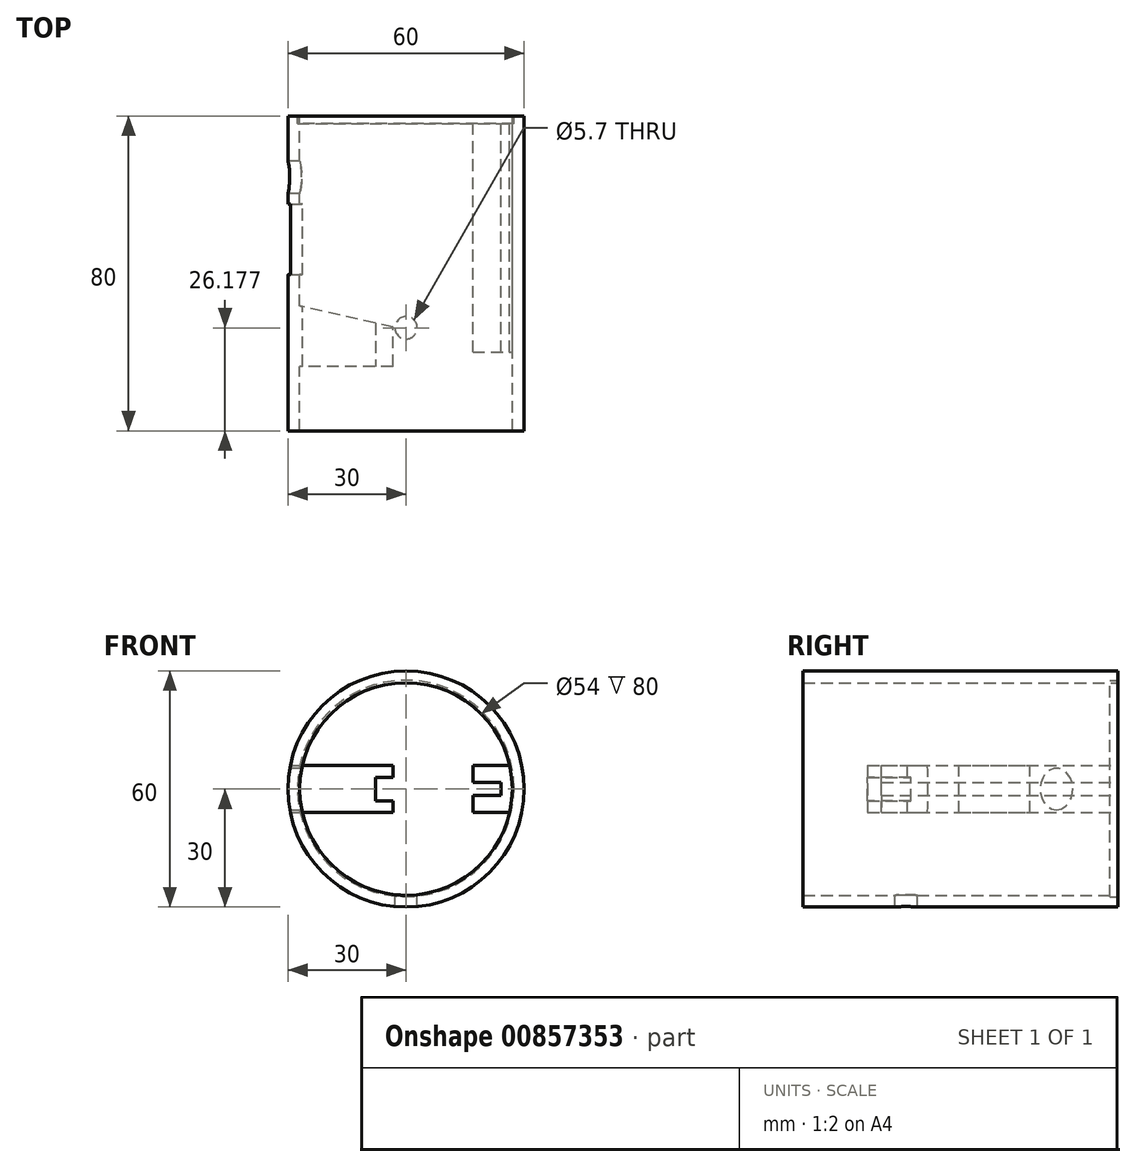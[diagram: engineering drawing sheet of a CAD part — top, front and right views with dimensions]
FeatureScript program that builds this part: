
annotation { "Feature Type Name" : "Feature", "Feature Type Description" : "" }
export const myFeature = defineFeature(function(context is Context, id is Id, definition is map)
    precondition{}
    {
        {
            var Q0;
            Q0=qCreatedBy(makeId("Front.planeOp"),FACE);
            var sketch = newSketch(context, id + "F0", { "sketchPlane" : qUnion([Q0])});
            skCircle(sketch, "E0", {"center": v(0, 0) * mm, "radius": 30 * mm});
            skCircle(sketch, "E1", {"center": v(0, 0) * mm, "radius": 27 * mm});
            skLineSegment(sketch, "E2.bottom", {"start": v(17, 0) * mm, "end": v(27, 0) * mm});
            skLineSegment(sketch, "E2.top", {"start": v(17, -6) * mm, "end": v(26.32, -6) * mm});
            skLineSegment(sketch, "E2.left", {"start": v(17, 0) * mm, "end": v(17, -6) * mm});
            skLineSegment(sketch, "E3.MirrorCS", {"start": v(17, 0) * mm, "end": v(17, 6) * mm});
            skLineSegment(sketch, "E4.MirrorCS", {"start": v(17, 6) * mm, "end": v(26.32, 6) * mm});
            skLineSegment(sketch, "E5.bottom", {"start": v(17, 0) * mm, "end": v(24.16, 0) * mm});
            skLineSegment(sketch, "E5.top", {"start": v(17, -1.62) * mm, "end": v(24.16, -1.62) * mm});
            skLineSegment(sketch, "E5.left", {"start": v(17, 0) * mm, "end": v(17, -1.62) * mm});
            skLineSegment(sketch, "E5.right", {"start": v(24.16, 0) * mm, "end": v(24.16, -1.62) * mm});
            skLineSegment(sketch, "E6.MirrorCS", {"start": v(17, 1.62) * mm, "end": v(24.16, 1.62) * mm});
            skLineSegment(sketch, "E7.MirrorCS", {"start": v(24.16, 0) * mm, "end": v(24.16, 1.62) * mm});
            skSolve(sketch);
        }
        {
            var Q0;
            Q0=makeQuery(id+"F0.imprint","IMPRINT",FACE,{"disambiguationData":[TD([[makeQuery(id+"F0.imprint","IMPRINT",EDGE,{"derivedFrom":sQuery(id+"F0.wireOp",EDGE,"E0")}),1.0]])]});
            extrude(context, id + "F1", {"entities" : qUnion([Q0]), "depth" : 80 * mm});
        }
        {
            var Q0;
            Q0=qCreatedBy(makeId("Front.planeOp"),FACE);
            var sketch = newSketch(context, id + "F2", { "sketchPlane" : qUnion([Q0])});
            skCircle(sketch, "E8", {"center": v(-0.08, 0.14) * mm, "radius": 27.5 * mm});
            skSolve(sketch);
        }
        {
            var Q0;
            Q0=makeQuery(id+"F2.imprint","IMPRINT",FACE,{"disambiguationData":[TD([[makeQuery(id+"F2.imprint","IMPRINT",EDGE,{"derivedFrom":sQuery(id+"F2.wireOp",EDGE,"E8")}),1.0]])]});
            extrude(context, id + "F3", {"entities" : qUnion([Q0]), "offsetDistance" : 25 * mm, "depth" : 2 * mm});
        }
        {
            var Q0;
            Q0=qCreatedBy(makeId("Top.planeOp"),FACE);
            var sketch = newSketch(context, id + "F4", { "sketchPlane" : qUnion([Q0])});
            skLineSegment(sketch, "E9.bottom", {"start": v(-32.36, -22.34) * mm, "end": v(-18.81, -22.34) * mm});
            skLineSegment(sketch, "E9.top", {"start": v(-32.36, -40.34) * mm, "end": v(-18.81, -40.34) * mm});
            skLineSegment(sketch, "E9.left", {"start": v(-32.36, -22.34) * mm, "end": v(-32.36, -40.34) * mm});
            skLineSegment(sketch, "E9.right", {"start": v(-18.81, -22.34) * mm, "end": v(-18.81, -40.34) * mm});
            skSolve(sketch);
        }
        {
            var Q0;
            Q0=makeQuery(id+"F4.imprint","IMPRINT",FACE,{"disambiguationData":[TD([[makeQuery(id+"F4.imprint","IMPRINT",EDGE,{"derivedFrom":sQuery(id+"F4.wireOp",EDGE,"E9.bottom")}),-1.0]])]});
            var Q1;
            Q1=qSketchRegion(id+"F6",true);
            extrude(context, id + "F5", {"entities" : qUnion([Q0, Q1]), "operationType" : NewBodyOperationType.REMOVE, "endBound" : BoundingType.SYMMETRIC, "depth" : 12 * mm, "hasSecondDirection" : true, "secondDirectionOppositeDirection" : true, "secondDirectionDepth" : 4.6 * mm});
        }
        {
            var Q0;
            Q0=qCreatedBy(makeId("Top.planeOp"),FACE);
            var sketch = newSketch(context, id + "F6", { "sketchPlane" : qUnion([Q0])});
            skCircle(sketch, "E10", {"center": v(0, -53.82) * mm, "radius": 2.85 * mm});
            skSolve(sketch);
        }
        {
            var Q0;
            Q0=makeQuery(id+"F6.imprint","IMPRINT",FACE,{"disambiguationData":[TD([[makeQuery(id+"F6.imprint","IMPRINT",EDGE,{"derivedFrom":sQuery(id+"F6.wireOp",EDGE,"E10")}),1.0]])]});
            var Q1;
            Q1=sQuery(id+"F6.wireOp",EDGE,"E10");
            extrude(context, id + "F7", {"entities" : qUnion([Q0]), "operationType" : NewBodyOperationType.REMOVE, "surfaceEntities" : qUnion([Q1]), "oppositeDirection" : true, "depth" : 34.4 * mm});
        }
        {
            var Q0;
            Q0=qCreatedBy(makeId("Top.planeOp"),FACE);
            var sketch = newSketch(context, id + "F8", { "sketchPlane" : qUnion([Q0])});
            skLineSegment(sketch, "E11.bottom", {"start": v(-3.31, -63.62) * mm, "end": v(-27.31, -63.62) * mm});
            skLineSegment(sketch, "E11.top", {"start": v(-3.31, -53.62) * mm, "end": v(-27.31, -53.62) * mm});
            skLineSegment(sketch, "E11.left", {"start": v(-3.31, -63.62) * mm, "end": v(-3.31, -53.62) * mm});
            skLineSegment(sketch, "E11.right", {"start": v(-27.31, -63.62) * mm, "end": v(-27.31, -53.62) * mm});
            skLineSegment(sketch, "E12", {"start": v(-3.31, -53.62) * mm, "end": v(-27.46, -48.22) * mm});
            skLineSegment(sketch, "E13", {"start": v(-27.46, -48.22) * mm, "end": v(-27.31, -53.62) * mm});
            skSolve(sketch);
        }
        {
            var Q0;
            Q0=makeQuery(id+"F8.imprint","IMPRINT",FACE,{"disambiguationData":[TD([[makeQuery(id+"F8.imprint","IMPRINT",EDGE,{"derivedFrom":sQuery(id+"F8.wireOp",EDGE,"E11.top")}),-1.0]])]});
            extrude(context, id + "F9", {"entities" : qUnion([Q0]), "operationType" : NewBodyOperationType.ADD, "endBound" : BoundingType.SYMMETRIC, "depth" : 12 * mm});
        }
        {
            var Q0;
            Q0=makeQuery(id+"F8.imprint","IMPRINT",FACE,{"disambiguationData":[TD([[makeQuery(id+"F8.imprint","IMPRINT",EDGE,{"derivedFrom":sQuery(id+"F8.wireOp",EDGE,"E11.bottom")}),-1.0]])]});
            extrude(context, id + "F10", {"entities" : qUnion([Q0]), "operationType" : NewBodyOperationType.ADD, "endBound" : BoundingType.SYMMETRIC, "depth" : 12 * mm});
        }
        {
            var Q0;
            Q0=qCreatedBy(makeId("Top.planeOp"),FACE);
            var sketch = newSketch(context, id + "F11", { "sketchPlane" : qUnion([Q0])});
            skLineSegment(sketch, "E14.bottom", {"start": v(-7.77, -49.01) * mm, "end": v(-2.6, -49.01) * mm});
            skLineSegment(sketch, "E14.top", {"start": v(-7.77, -67.01) * mm, "end": v(-2.6, -67.01) * mm});
            skLineSegment(sketch, "E14.left", {"start": v(-7.77, -49.01) * mm, "end": v(-7.77, -67.01) * mm});
            skLineSegment(sketch, "E14.right", {"start": v(-2.6, -49.01) * mm, "end": v(-2.6, -67.01) * mm});
            skSolve(sketch);
        }
        {
            var Q0;
            Q0=qSketchRegion(id+"F11",true);
            extrude(context, id + "F12", {"entities" : qUnion([Q0]), "operationType" : NewBodyOperationType.REMOVE, "endBound" : BoundingType.SYMMETRIC, "depth" : 6 * mm});
        }
        {
            var Q0;
            {var subQ0=sQuery(id+"F0.wireOp",EDGE,"E4.MirrorCS");Q0=makeQuery(id+"F0.imprint","IMPRINT",FACE,{"disambiguationData":[TD([[makeQuery(id+"F0.imprint","IMPRINT",EDGE,{"derivedFrom":subQ0}),-1.0]])]});}
            var Q1;
            {var subQ1=sQuery(id+"F0.wireOp",EDGE,"E2.top");Q1=makeQuery(id+"F0.imprint","IMPRINT",FACE,{"disambiguationData":[TD([[makeQuery(id+"F0.imprint","IMPRINT",EDGE,{"derivedFrom":subQ1}),1.0]])]});}
            extrude(context, id + "F13", {"entities" : qUnion([Q0, Q1]), "depth" : 60 * mm});
        }
        {
            var Q0;
            Q0=qCreatedBy(makeId("Right.planeOp"),FACE);
            var sketch = newSketch(context, id + "F14", { "sketchPlane" : qUnion([Q0])});
            skEllipse(sketch, "E15", {"center": v(-15.58, 0) * mm, "majorRadius": 5.25 * mm, "minorRadius": 4.16 * mm, "majorAxis": v(0, -1)});
            skSolve(sketch);
        }
        {
            var Q0;
            Q0=qSketchRegion(id+"F14",true);
            extrude(context, id + "F15", {"entities" : qUnion([Q0]), "operationType" : NewBodyOperationType.REMOVE, "oppositeDirection" : true, "depth" : 50 * mm});
        }
    });
